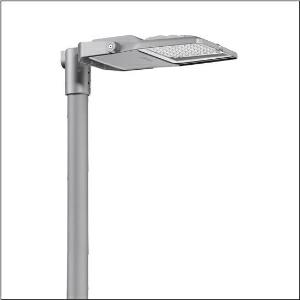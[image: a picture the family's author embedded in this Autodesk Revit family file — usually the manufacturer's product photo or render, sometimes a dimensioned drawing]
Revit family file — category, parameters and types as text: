
# Revit family: floodlight_fl_21_iq_mini___pl52_5xa7771d4d3a_bc98
name_source: partatom
category: Lighting Fixtures
units: mm (PartAtom-declared; Revit-internal decimal feet)

## family parameters
Cut with Voids When Loaded = No
Host = Face
Light Source = No
Part Type = Normal
Room Calculation Point = No
Round Connector Dimension = Use Diameter
Shared = No

## types (1)
- --- (1 x LED, 18610 lm, 143 W, 4000K)
    Apparent Load = 143 VA
    CIE Flux Codes = 26 60 98 100 100
    Color Rendering = 70
    Color Temperature = 4000K
    Default Elevation = 1800 mm
    Description = Floodlight FL 21 iQ mini, floodlight, primary light control with lens, of PMMA, primary optical cover: protective disc, of toughened safety glass, transparent, light distribution: PL52, light emission: direct distribution, installation type: surface-mounted, lamps: LED, High Power LED, rated values: 18.610lm | 143W | 130,1lm/W (begin service life); end service life: 18.610lm | 151,6W; at 50% lumin. flux: 9.305lm | 60,8W | 153lm/W, colour temperature: 4000K, colour rendering: CRI > 70, light colour: 740, light setting 1 begin service life: 100% | 18.610lm | 143W | 130,1lm/W | 4.000K, light setting 1 end service life: 151,6W, further light settings possible, control: Auto-Match, Temp-Guard, Lumen-Switch, Night-Set, Smart-Wire, Light-Fading, Desk-Remote (wireless, voltage-free reading and setting of iQ features in the workshop via application-optimized NFC function/RFID function), optimised constant luminous flux control (CLO 2.0), pre-setting: linear dimming characteristic, with terminal, 6-pole, mains connection: 220..240V, AC, 50/60Hz, luminaire housing, of diecast aluminium, powder-coated, SITECO metallic grey (DB 702S), corrosivity category C5 mid according to DIN EN ISO 12944suitable for swimming poolschlorine-resistant, sealing non-destructively replaceable, please order mast flange separately, mast bracket, of steel, galvanised, powder-coated, SITECO metallic grey (DB 702S), protection rating (complete): IP66, insulation class (complete): insulation class II (safety insulation), certification: CE, ENEC, VDE, protection symbol: D, impact resistance: IK08, permissible operating ambient temperature: -40..+40°C, permissible operating ambient temperature for outdoor applications: -40..+50°C, standard: DIN EN 12944, LABS conformity tested according to VDMA 24364:2018-05, packaging unit: 1 piece

Light Distribution: PL52
    Height = 70 mm
    Lamp = 1 x LED
    Lamp Light Flux = 18610 lm
    Lamp Power = 143 W
    Lamp count = 1
    Length = 485 mm
    Luminous efficacy = 130 lm/W
    Manufacturer = Siteco
    ModVariant = No
    Model = 5XA7771D4D3A
    Mounting Place = Pole
    Mounting Type = Pole annexe
    Number of Poles = 1
    OnlyDefault = Yes
    Power Factor = 1
    Product Name = Floodlight FL 21 iQ mini | PL52
    Product group = floodlight | pylon annexe
    ProductGroupID = 6201
    Protection Class = Protection class II
    Protection Degree = IP 66
    RLX_Detail_Level = 1
    RLX_Emergency_Light_Flux = 0 lm
    RLX_Emergency_Type = 0
    RLX_Emergency_Type_DB = No
    RlxData = <blob elided: 101997 chars, md5=214606df>
    Socket = socket
    Standby Power = 0 W
    System Light Flux = 18610 lm
    System Power = 143 W
    Type Comments = factory setting: luminous flux: 100 % | dim-lin: 254 | 730 mA
    Type Image = l_1007125.jpg
    URL = http://relux.com
    VarID = @adj_164889
    Voltage = 0 V
    Weight = 0.00 kg
    Width = 337 mm

## geometry (parser evidence)
native form markers: Blend x4, Sweep x11
no freeform markers — native parametric forms only
